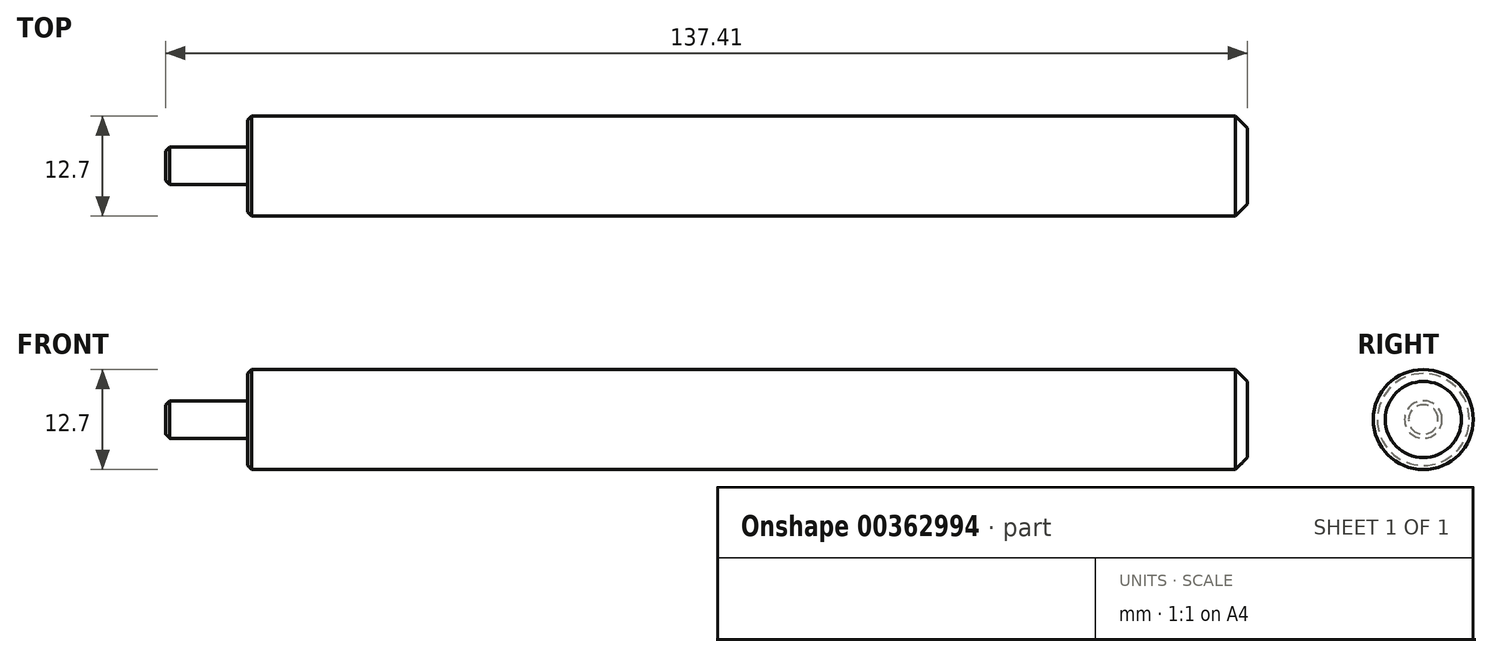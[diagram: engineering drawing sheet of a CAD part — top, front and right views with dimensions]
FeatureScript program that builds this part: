
annotation { "Feature Type Name" : "Feature", "Feature Type Description" : "" }
export const myFeature = defineFeature(function(context is Context, id is Id, definition is map)
    precondition{}
    {
        {
            var Q0;
            Q0=qCreatedBy(makeId("Right.planeOp"),FACE);
            var sketch = newSketch(context, id + "F0", { "sketchPlane" : qUnion([Q0])});
            skCircle(sketch, "E0", {"center": v(0, 0) * mm, "radius": 6.35 * mm});
            skSolve(sketch);
        }
        {
            var Q0;
            Q0=makeQuery(id+"F0.imprint","IMPRINT",FACE,{"disambiguationData":[TD([[makeQuery(id+"F0.imprint","IMPRINT",EDGE,{"derivedFrom":sQuery(id+"F0.wireOp",EDGE,"E0")}),1.0]])]});
            extrude(context, id + "F1", {"entities" : qUnion([Q0]), "depth" : 127 * mm});
        }
        {
            var Q0;
            Q0=makeQuery(id+"F1.opExtrude","CAP_EDGE",EDGE,{"disambiguationData":[OSD([sQuery(id+"F0.wireOp",EDGE,"E0")])],"isStart":false});
            chamfer(context, id + "F2", {"entities" : qUnion([Q0]), "chamferType" : ChamferType.OFFSET_ANGLE, "width" : 1.52 * mm, "oppositeDirection" : false, "angle" : 45 * degree, "tangentPropagation" : true});
        }
        {
            var Q0;
            Q0=qCreatedBy(makeId("Right.planeOp"),FACE);
            var sketch = newSketch(context, id + "F3", { "sketchPlane" : qUnion([Q0])});
            skCircle(sketch, "E1", {"center": v(0, 0) * mm, "radius": 2.38 * mm});
            skSolve(sketch);
        }
        {
            var Q0;
            Q0=makeQuery(id+"F3.imprint","IMPRINT",FACE,{"disambiguationData":[TD([[makeQuery(id+"F3.imprint","IMPRINT",EDGE,{"derivedFrom":sQuery(id+"F3.wireOp",EDGE,"E1")}),1.0]])]});
            extrude(context, id + "F4", {"entities" : qUnion([Q0]), "operationType" : NewBodyOperationType.ADD, "oppositeDirection" : true, "depth" : 10.4 * mm});
        }
        {
            var Q0;
            Q0=makeQuery(id+"F1.opExtrude","CAP_EDGE",EDGE,{"disambiguationData":[OSD([sQuery(id+"F0.wireOp",EDGE,"E0")])],"isStart":true});
            var Q1;
            Q1=makeQuery(id+"F4.opExtrude","CAP_EDGE",EDGE,{"disambiguationData":[OSD([sQuery(id+"F3.wireOp",EDGE,"E1")])],"isStart":false});
            chamfer(context, id + "F5", {"entities" : qUnion([Q0, Q1]), "chamferType" : ChamferType.OFFSET_ANGLE, "width" : 0.5 * mm, "oppositeDirection" : false, "angle" : 45 * degree, "tangentPropagation" : true});
        }
    });
